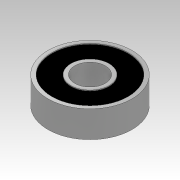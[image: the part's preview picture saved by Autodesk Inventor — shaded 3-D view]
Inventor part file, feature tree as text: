
AUTODESK INVENTOR PART (.ipt)
format: ipt  version: 2020 (Build 240168000, 168)  size: 127,488 bytes
history: native  units: mm
features: revolve x1, sketch x1
ambient origin geometry x8: Origin, YZ Plane, XZ Plane, XY Plane, X Axis, Y Axis, Z Axis, Center Point
bodies: Solid1 (feature_tree)
feature tree (2):
  revolve  "Revolution1"  [1 undecoded]
  sketch  "Sketch1"  dims[d0=4.0mm d2=7.0mm d5=11.0mm d6=0.2mm d7=1.0mm d8=90.0deg]
note: 1 required parameter value undecoded (feature->parameter linkage not recoverable at this tier; creation-order binding heuristic only, values carry confidence <= 0.55)
